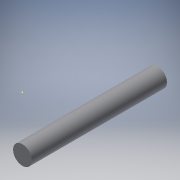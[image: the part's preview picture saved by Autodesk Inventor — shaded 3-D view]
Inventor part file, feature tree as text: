
AUTODESK INVENTOR PART (.ipt)
format: ipt  version: 2019 (Build 230136000, 136)  size: 107,520 bytes
history: native  units: mm
features: sketch x2, extrude x1
ambient origin geometry x8: Origin, YZ Plane, XZ Plane, XY Plane, X Axis, Y Axis, Z Axis, Center Point
bodies: Solid1 (feature_tree)
feature tree (3):
  extrude  "Extrusion1"  Depth=28.0mm
  sketch  "Sketch2"  dims[d2=22.0mm d3=14.5mm d4=4.0mm d5=28.0mm d6=28.0mm d7=5.0mm d8=36.0mm d9=0.0mm]
  sketch  "Sketch1"  dims[d0=14.0mm d1=28.0mm]
